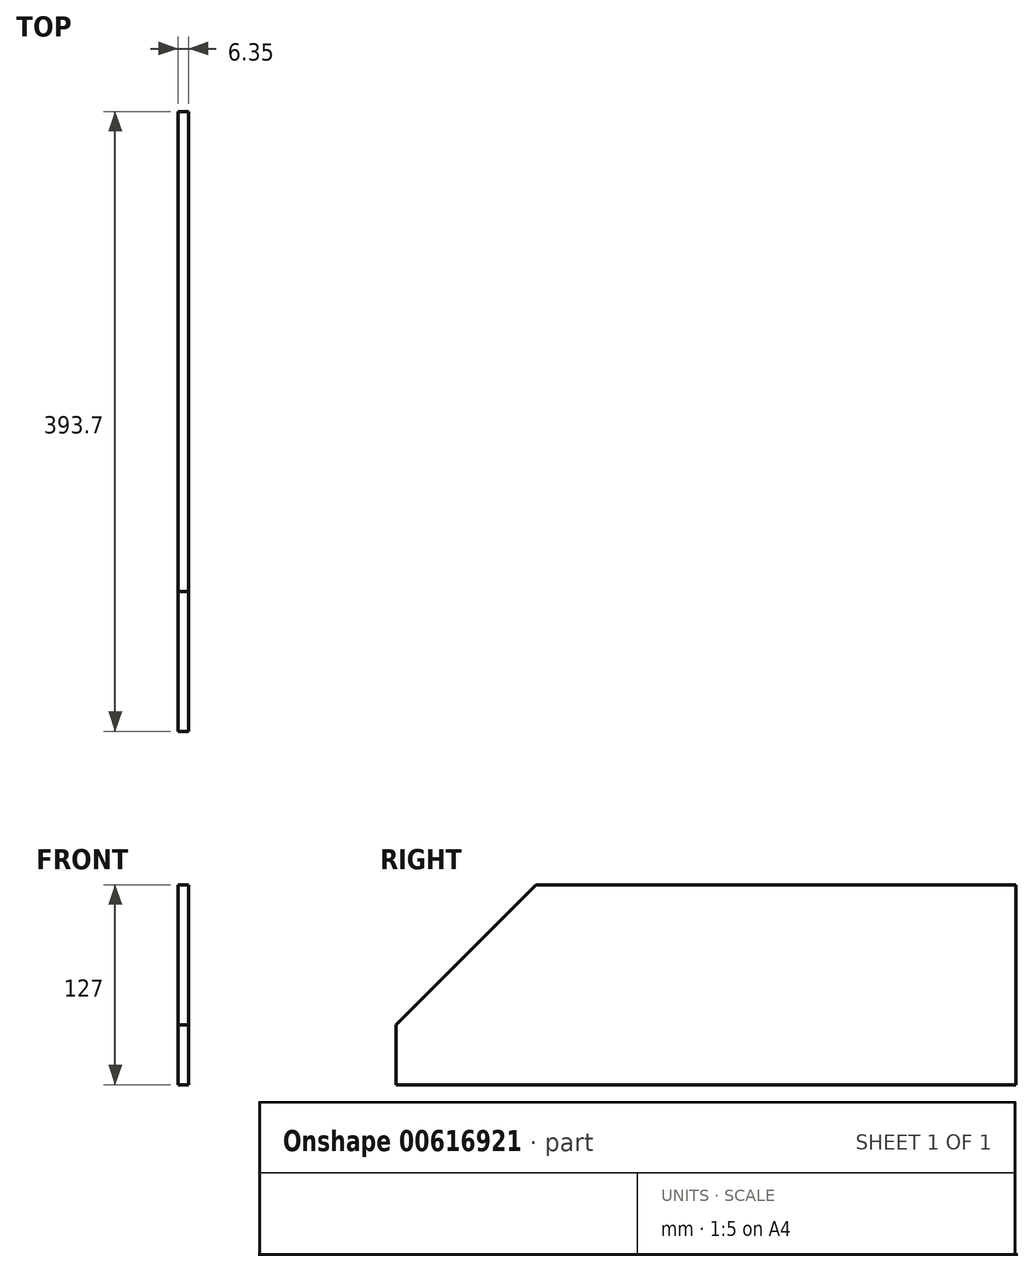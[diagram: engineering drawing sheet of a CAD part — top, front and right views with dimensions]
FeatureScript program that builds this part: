
annotation { "Feature Type Name" : "Feature", "Feature Type Description" : "" }
export const myFeature = defineFeature(function(context is Context, id is Id, definition is map)
    precondition{}
    {
        {
            var Q0;
            Q0=qCreatedBy(makeId("Right.planeOp"),FACE);
            var sketch = newSketch(context, id + "F0", { "sketchPlane" : qUnion([Q0])});
            skLineSegment(sketch, "E0", {"start": v(-196.85, 0) * mm, "end": v(196.85, 0) * mm});
            skLineSegment(sketch, "E1", {"start": v(196.85, 0) * mm, "end": v(196.85, 127) * mm});
            skLineSegment(sketch, "E2", {"start": v(196.85, 127) * mm, "end": v(-107.95, 127) * mm});
            skLineSegment(sketch, "E3", {"start": v(-107.95, 127) * mm, "end": v(-196.85, 38.1) * mm});
            skLineSegment(sketch, "E4", {"start": v(-196.85, 38.1) * mm, "end": v(-196.85, 0) * mm});
            skLineSegment(sketch, "E5", {"start": v(-107.95, 127) * mm, "end": v(-107.95, 0) * mm, "construction": true});
            skSolve(sketch);
        }
        {
            var Q0;
            Q0 = qSketchRegion(id + "F0", true);
            extrude(context, id + "F1", {"entities" : qUnion([Q0]), "depth" : 6.35 * mm, "offsetDistance" : 25.4 * mm});
        }
    });
